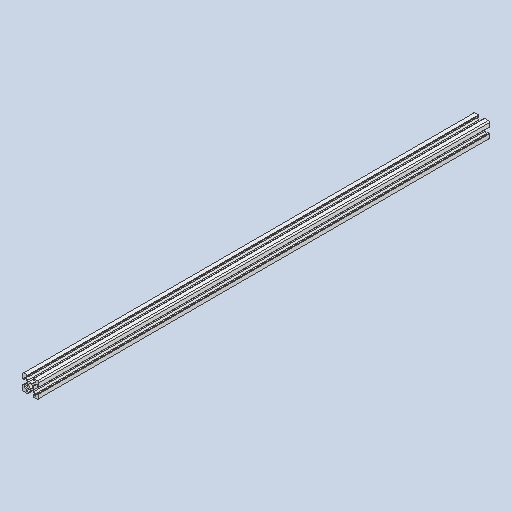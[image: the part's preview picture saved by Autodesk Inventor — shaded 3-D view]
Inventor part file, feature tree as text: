
AUTODESK INVENTOR PART (.ipt)
format: ipt  version: 2023 (Build 270158000, 158)  size: 253,952 bytes
history: native  units: mm
features: extrude x1, sketch x1, projected_geometry x1
ambient origin geometry x8: Origin, YZ Plane, XZ Plane, XY Plane, X Axis, Y Axis, Z Axis, Center Point
bodies: Solid1 (feature_tree), Body1 (feature_tree)
feature tree (3):
  extrude  "Extrusion1"  [1 undecoded]
  sketch  "Sketch1"  dims[d0=460.0mm d1=0.0mm]
  projected_geometry  "Projected Loop1"
note: 1 required parameter value undecoded (feature->parameter linkage not recoverable at this tier; creation-order binding heuristic only, values carry confidence <= 0.55)
